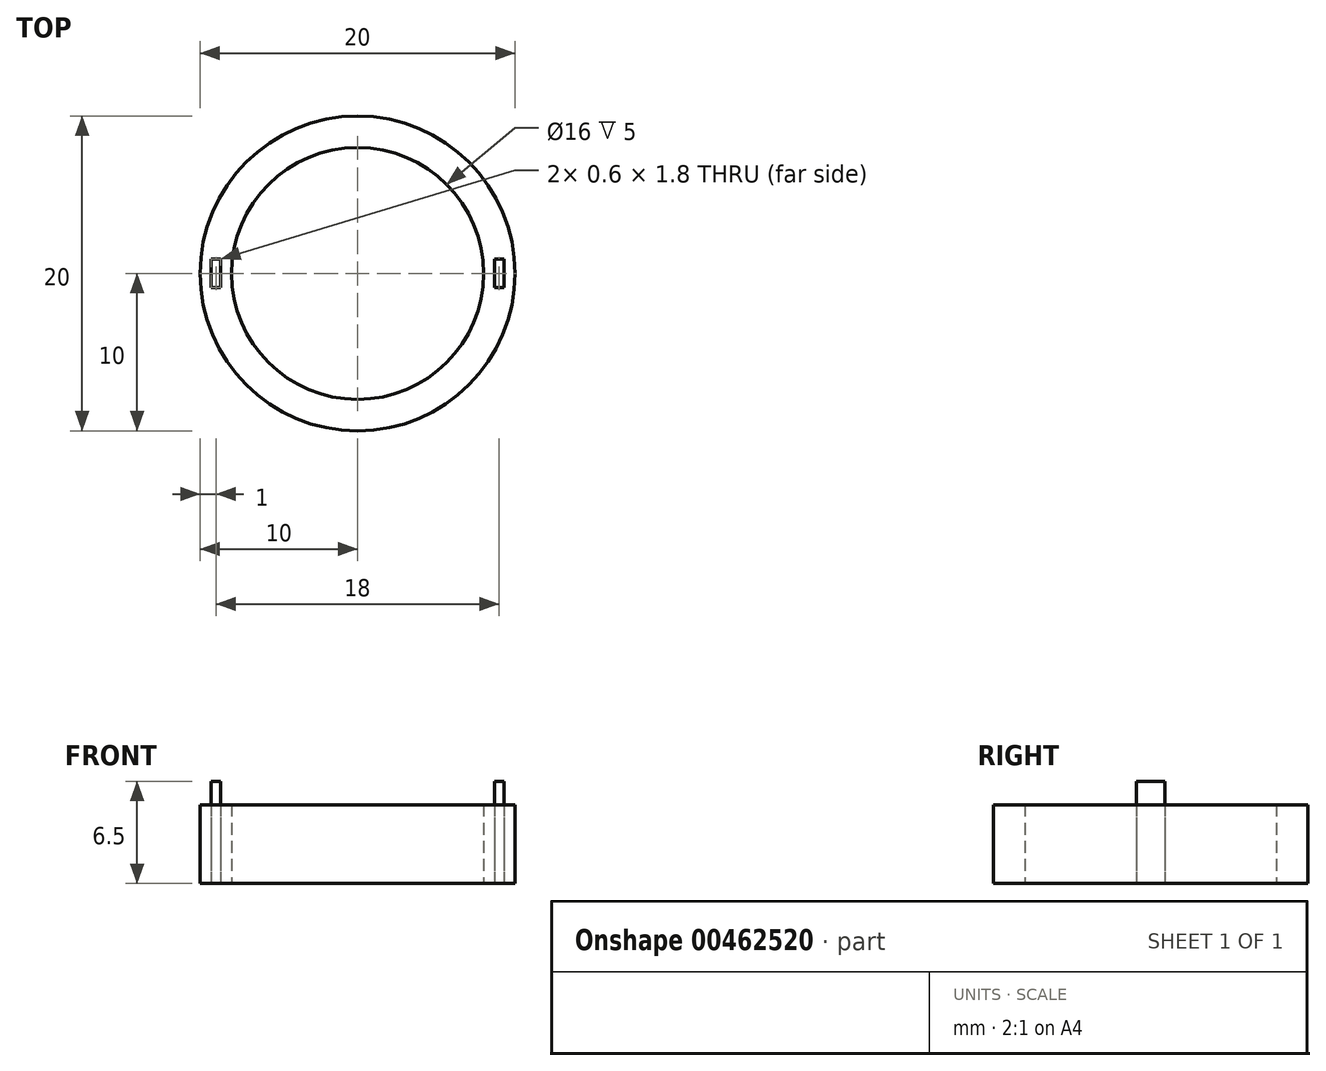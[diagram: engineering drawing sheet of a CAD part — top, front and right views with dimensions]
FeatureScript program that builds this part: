
annotation { "Feature Type Name" : "Feature", "Feature Type Description" : "" }
export const myFeature = defineFeature(function(context is Context, id is Id, definition is map)
    precondition{}
    {
        {
            var Q0;
            Q0=qCreatedBy(makeId("Top.planeOp"),FACE);
            var sketch = newSketch(context, id + "F0", { "sketchPlane" : qUnion([Q0])});
            skCircle(sketch, "E0", {"center": v(0, 0) * mm, "radius": 10 * mm});
            skCircle(sketch, "E1", {"center": v(0, 0) * mm, "radius": 8 * mm});
            skLineSegment(sketch, "E2.bottom", {"start": v(-9.3, 0.9) * mm, "end": v(-8.7, 0.9) * mm});
            skLineSegment(sketch, "E2.top", {"start": v(-9.3, -0.9) * mm, "end": v(-8.7, -0.9) * mm});
            skLineSegment(sketch, "E2.left", {"start": v(-9.3, 0.9) * mm, "end": v(-9.3, -0.9) * mm});
            skLineSegment(sketch, "E2.right", {"start": v(-8.7, 0.9) * mm, "end": v(-8.7, -0.9) * mm});
            skLineSegment(sketch, "E3.bottom", {"start": v(8.7, 0.9) * mm, "end": v(9.3, 0.9) * mm});
            skLineSegment(sketch, "E3.top", {"start": v(8.7, -0.9) * mm, "end": v(9.3, -0.9) * mm});
            skLineSegment(sketch, "E3.left", {"start": v(8.7, 0.9) * mm, "end": v(8.7, -0.9) * mm});
            skLineSegment(sketch, "E3.right", {"start": v(9.3, 0.9) * mm, "end": v(9.3, -0.9) * mm});
            skSolve(sketch);
        }
        {
            var Q0;
            Q0=makeQuery(id+"F0.imprint","IMPRINT",FACE,{"disambiguationData":[TD([[makeQuery(id+"F0.imprint","IMPRINT",EDGE,{"derivedFrom":sQuery(id+"F0.wireOp",EDGE,"E2.bottom")}),-1.0]])]});
            var Q1;
            Q1=makeQuery(id+"F0.imprint","IMPRINT",FACE,{"disambiguationData":[TD([[makeQuery(id+"F0.imprint","IMPRINT",EDGE,{"derivedFrom":sQuery(id+"F0.wireOp",EDGE,"E3.bottom")}),-1.0]])]});
            extrude(context, id + "F1", {"entities" : qUnion([Q0, Q1]), "depth" : 6.5 * mm});
        }
        {
            var Q0;
            Q0=qSketchRegion(id+"F0",true);
            extrude(context, id + "F2", {"entities" : qUnion([Q0]), "depth" : 5 * mm});
        }
    });
